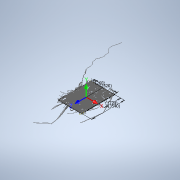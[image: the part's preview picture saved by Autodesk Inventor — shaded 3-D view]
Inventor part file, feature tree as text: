
AUTODESK INVENTOR PART (.ipt)
format: ipt  version: 2021 (Build 250183000, 183)  size: 22,614,016 bytes
history: native  units: mm
features: other x42, surface_op x2, sketch x1
ambient origin geometry x8: Origin, YZ Plane, XZ Plane, XY Plane, X Axis, Y Axis, Z Axis, Center Point
feature tree (45):
  other  "ciudadLeon"
  other  "SCU1"
  sketch  "Boceto1"  dims[d0=0.0mm d1=0.0mm d2=0.0mm d3=0.0mm d4=0.0mm d5=0.0mm d6=2520000.0mm d7=3540000.0mm d9=1260000.0mm d10=1770000.0mm]
  other  "RoadJunction"
  other  "RoadCrossingAtConnector"
  other  "BuildingEntrance"
  other  "Tree"
  other  "RecyclingContainer"
  other  "BusStop"
  other  "HighVoltagePowerTower"
  other  "RoadConnector"
  other  "Bench"
  other  "StreetLamp"
  other  "Flagpole"
  other  "Cross"
  other  "Bollard"
  other  "Wall"
  other  "Road"
  other  "Tunnel"
  other  "RetainingWall"
  other  "PoleFence"
  other  "Bridge"
  other  "Rail"
  other  "TreeRow"
  other  "CityWall"
  other  "Hedge"
  other  "Waterway"
  other  "PowerLine"
  other  "RoadArea"
  other  "Building"
  surface_op  "SurfaceArea"
  other  "Water"
  other  "AreaFountain"
  surface_op  "SurfaceParking"
  other  "Pool"
  other  "TennisPitch"
  other  "SoccerPitch"
  other  "Forest"
  other  "SCU1: Plano YZ"
  other  "SCU1: Plano XZ"
  other  "SCU1: Plano XY"
  other  "SCU1: Eje X"
  other  "SCU1: Eje Y"
  other  "SCU1: Eje Z"
  other  "SCU1: Centro"
